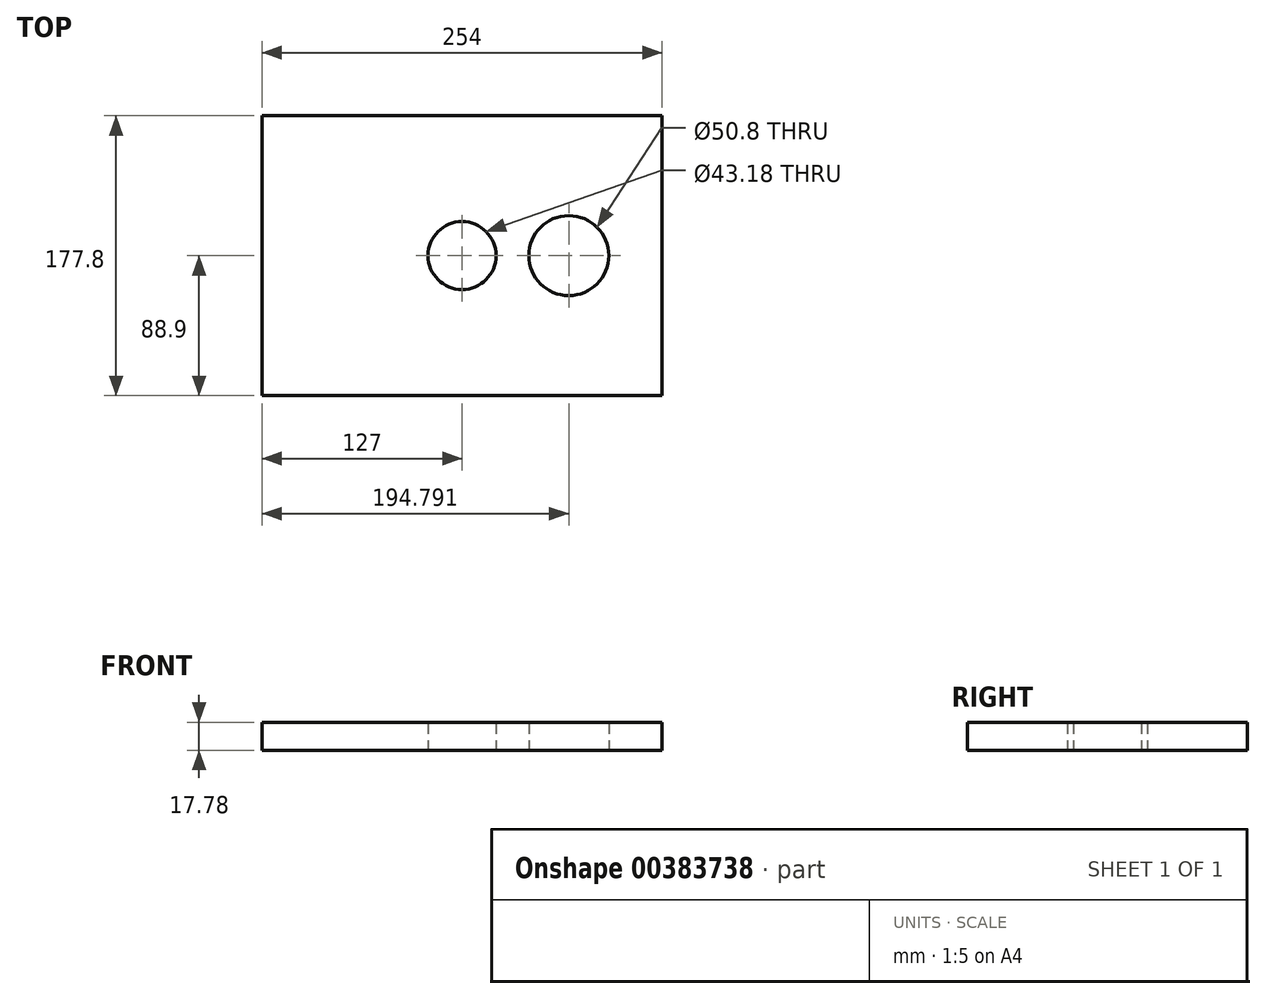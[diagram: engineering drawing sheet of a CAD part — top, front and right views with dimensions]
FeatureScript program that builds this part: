
annotation { "Feature Type Name" : "Feature", "Feature Type Description" : "" }
export const myFeature = defineFeature(function(context is Context, id is Id, definition is map)
    precondition{}
    {
        {
            var Q0;
            Q0=qCreatedBy(makeId("Top.planeOp"),FACE);
            var sketch = newSketch(context, id + "F0", { "sketchPlane" : qUnion([Q0])});
            skLineSegment(sketch, "E0.bottom", {"start": v(-127, 88.9) * mm, "end": v(127, 88.9) * mm});
            skLineSegment(sketch, "E0.top", {"start": v(-127, -88.9) * mm, "end": v(127, -88.9) * mm});
            skLineSegment(sketch, "E0.left", {"start": v(-127, 88.9) * mm, "end": v(-127, -88.9) * mm});
            skLineSegment(sketch, "E0.right", {"start": v(127, 88.9) * mm, "end": v(127, -88.9) * mm});
            skPoint(sketch, "E0.middle", {"position": v(0, 0) * mm});
            skCircle(sketch, "E1", {"center": v(67.8, 0) * mm, "radius": 25.4 * mm});
            skCircle(sketch, "E2", {"center": v(0, 0) * mm, "radius": 21.59 * mm});
            skSolve(sketch);
        }
        {
            var Q0;
            Q0=makeQuery(id+"F0.imprint","IMPRINT",FACE,{"disambiguationData":[TD([[makeQuery(id+"F0.imprint","IMPRINT",EDGE,{"derivedFrom":sQuery(id+"F0.wireOp",EDGE,"E0.bottom")}),-1.0]])]});
            extrude(context, id + "F1", {"entities" : qUnion([Q0]), "depth" : 17.78 * mm});
        }
    });
